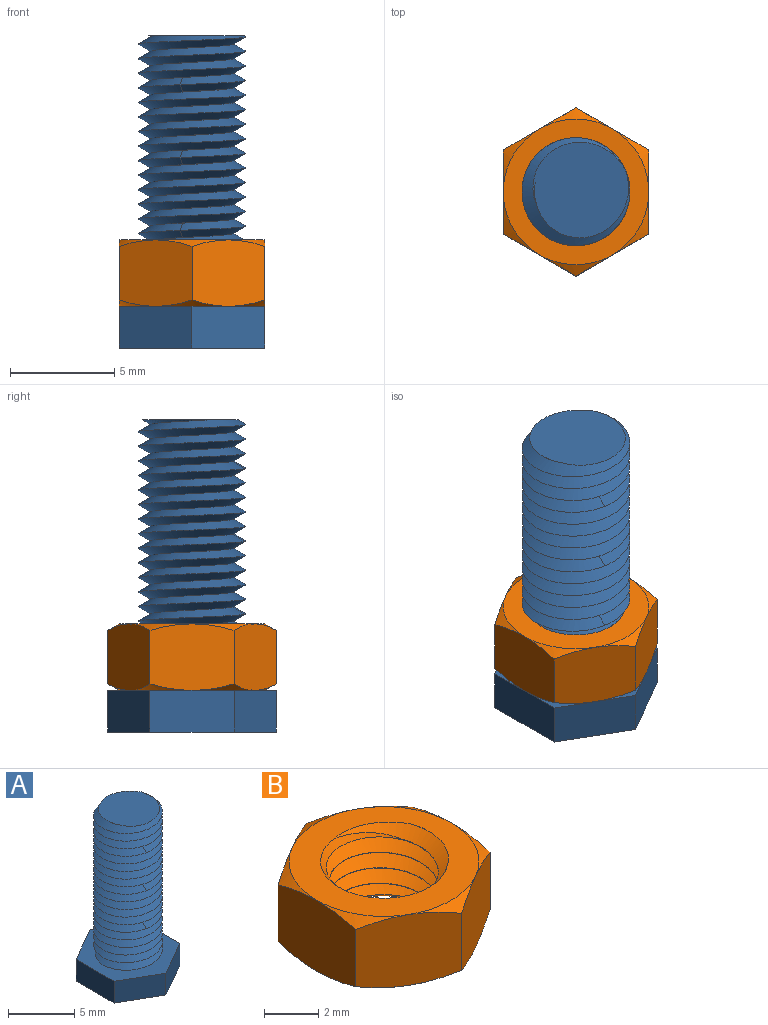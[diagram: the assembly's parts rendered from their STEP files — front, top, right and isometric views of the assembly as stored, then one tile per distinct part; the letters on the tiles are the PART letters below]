
ASSEMBLY  parts=2 mates=1
PART A: 18 faces, bbox 7.5x8.6x15.9 mm
  f0: cylinder r=2mm len=13mm, axis (0,0,-1), area 4.2mm2, adj f1,f2,f3,f4,f5,f6,f7,f8
  f1: plane 5.09x5.09mm, normal (0,0,1), area 16.6mm2, adj f0,f2,f3
  f2: bspline ~5.99x5.19mm, area 35.5mm2, adj f0,f1,f3,f8
  f3: bspline ~5.99x5.19mm, area 30.8mm2, adj f0,f1,f2,f9
  f4: bspline ~5.99x5.19mm, area 54mm2, adj f0,f5,f7,f10
  f5: bspline ~5.99x5.19mm, area 49.4mm2, adj f0,f4,f6,f10
  f6: bspline ~5.99x5.19mm, area 49.5mm2, adj f0,f5,f7,f8
  f7: bspline ~5.99x5.19mm, area 49.5mm2, adj f0,f4,f6,f9
  f8: bspline ~5.99x5.19mm, area 49.5mm2, adj f0,f2,f6,f9
  f9: bspline ~5.99x5.19mm, area 49.5mm2, adj f0,f3,f7,f8
  f10: plane 8.55x7.47mm, normal (0,0,1), area 25.9mm2, adj f0,f4,f5,f11,f12,f13,f14,f15
  f11: plane 4.04x2mm, normal (1,0,0), area 8.1mm2, adj f10,f12,f16,f17
  f12: plane 3.5x2.02mm, normal (0.5,0.87,0), area 8.1mm2, adj f10,f11,f13,f17
  f13: plane 3.5x2.02mm, normal (-0.5,0.87,0), area 8.1mm2, adj f10,f12,f14,f17
  f14: plane 4.04x2mm, normal (-1,0,0), area 8.1mm2, adj f10,f13,f15,f17
  f15: plane 3.5x2.02mm, normal (-0.5,-0.87,0), area 8.1mm2, adj f10,f14,f16,f17
  f16: plane 3.5x2.02mm, normal (0.5,-0.87,0), area 8.1mm2, adj f10,f11,f15,f17
  f17: plane 8.08x7mm, normal (0,0,-1), area 42.4mm2, adj f11,f12,f13,f14,f15,f16
PART B: 25 faces, bbox 8.4x8.4x4.4 mm
  f0: plane 3.83x3.54mm, normal (0.5,-0.87,0), area 12.1mm2, adj f1,f5,f13,f14,f15,f16
  f1: plane 4.38x3.54mm, normal (1,0,0), area 12.1mm2, adj f0,f2,f9,f14,f15,f20
  f2: plane 3.83x3.54mm, normal (0.5,0.87,0), area 12.1mm2, adj f1,f3,f9,f10,f19,f20
  f3: plane 3.83x3.54mm, normal (-0.5,0.87,0), area 12.1mm2, adj f2,f4,f10,f11,f18,f19
  f4: plane 4.38x3.54mm, normal (-1,0,0), area 12.1mm2, adj f3,f5,f11,f12,f17,f18
  f5: plane 3.83x3.54mm, normal (-0.5,-0.87,0), area 12.1mm2, adj f0,f4,f12,f13,f16,f17
  f6: plane 7.12x7.12mm, normal (0,0,-1), area 20.5mm2, adj f15,f16,f17,f18,f19,f20,f22,f23
  f7: plane 7.1x7.1mm, normal (0,0,1), area 20.5mm2, adj f9,f10,f11,f12,f13,f14,f21,f23
  f8: cylinder r=2mm len=4mm, axis (0,0,-1), area 1mm2, adj f21,f22,f23,f24
  f9: cone r=3.5mm half-angle=60deg, axis (0,0,-1), area 1.2mm2, adj f1,f2,f7
  f10: cone r=3.5mm half-angle=60deg, axis (0,0,-1), area 1.2mm2, adj f2,f3,f7
  f11: cone r=3.5mm half-angle=60deg, axis (0,0,-1), area 1.2mm2, adj f3,f4,f7
  f12: cone r=3.5mm half-angle=60deg, axis (0,0,-1), area 1.2mm2, adj f4,f5,f7
  f13: cone r=3.5mm half-angle=60deg, axis (0,0,-1), area 1.2mm2, adj f0,f5,f7
  f14: cone r=3.5mm half-angle=60deg, axis (0,0,-1), area 1.2mm2, adj f0,f1,f7
  f15: cone r=3.5mm half-angle=60deg, axis (0,0,1), area 1.2mm2, adj f0,f1,f6
  f16: cone r=3.5mm half-angle=60deg, axis (0,0,1), area 1.2mm2, adj f0,f5,f6
  f17: cone r=3.5mm half-angle=60deg, axis (0,0,1), area 1.2mm2, adj f4,f5,f6
  f18: cone r=3.5mm half-angle=60deg, axis (0,0,1), area 1.2mm2, adj f3,f4,f6
  f19: cone r=3.5mm half-angle=60deg, axis (0,0,1), area 1.2mm2, adj f2,f3,f6
  f20: cone r=3.5mm half-angle=60deg, axis (0,0,1), area 1.2mm2, adj f1,f2,f6
  f21: cone r=2mm half-angle=45deg, axis (0,0,1), area 2mm2, adj f7,f8,f23,f24
  f22: cone r=2.34mm half-angle=45deg, axis (0,0,-1), area 2mm2, adj f6,f8,f23,f24
  f23: bspline ~5.99x5.19mm, area 42.8mm2, adj f6,f7,f8,f21,f22,f24
  f24: bspline ~5.99x5.19mm, area 42.8mm2, adj f6,f7,f8,f21,f22,f23
PLACE A at identity fixed
PLACE B at identity
MATE cylindrical A.f0 <-> B.f8  axis (0,0,1) through (0,0,0)mm
